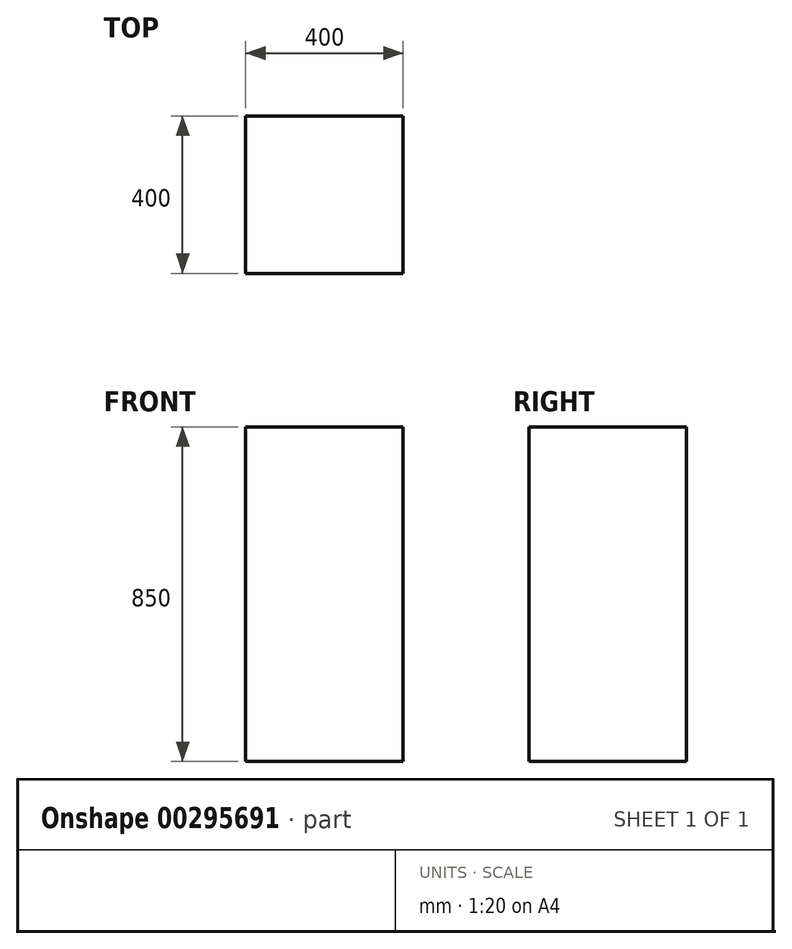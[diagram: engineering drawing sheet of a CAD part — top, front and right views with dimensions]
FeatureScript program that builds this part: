
annotation { "Feature Type Name" : "Feature", "Feature Type Description" : "" }
export const myFeature = defineFeature(function(context is Context, id is Id, definition is map)
    precondition{}
    {
        {
            var Q0;
            Q0=qCreatedBy(makeId("Front.planeOp"),FACE);
            var sketch = newSketch(context, id + "F0", { "sketchPlane" : qUnion([Q0])});
            skLineSegment(sketch, "E0.bottom", {"start": v(0, 0) * mm, "end": v(400, 0) * mm});
            skLineSegment(sketch, "E0.top", {"start": v(0, 850) * mm, "end": v(400, 850) * mm});
            skLineSegment(sketch, "E0.left", {"start": v(0, 0) * mm, "end": v(0, 850) * mm});
            skLineSegment(sketch, "E0.right", {"start": v(400, 0) * mm, "end": v(400, 850) * mm});
            skSolve(sketch);
        }
        {
            var Q0;
            Q0 = qSketchRegion(id + "F0", true);
            extrude(context, id + "F1", {"entities" : qUnion([Q0]), "oppositeDirection" : true, "depth" : 400 * mm});
        }
    });
